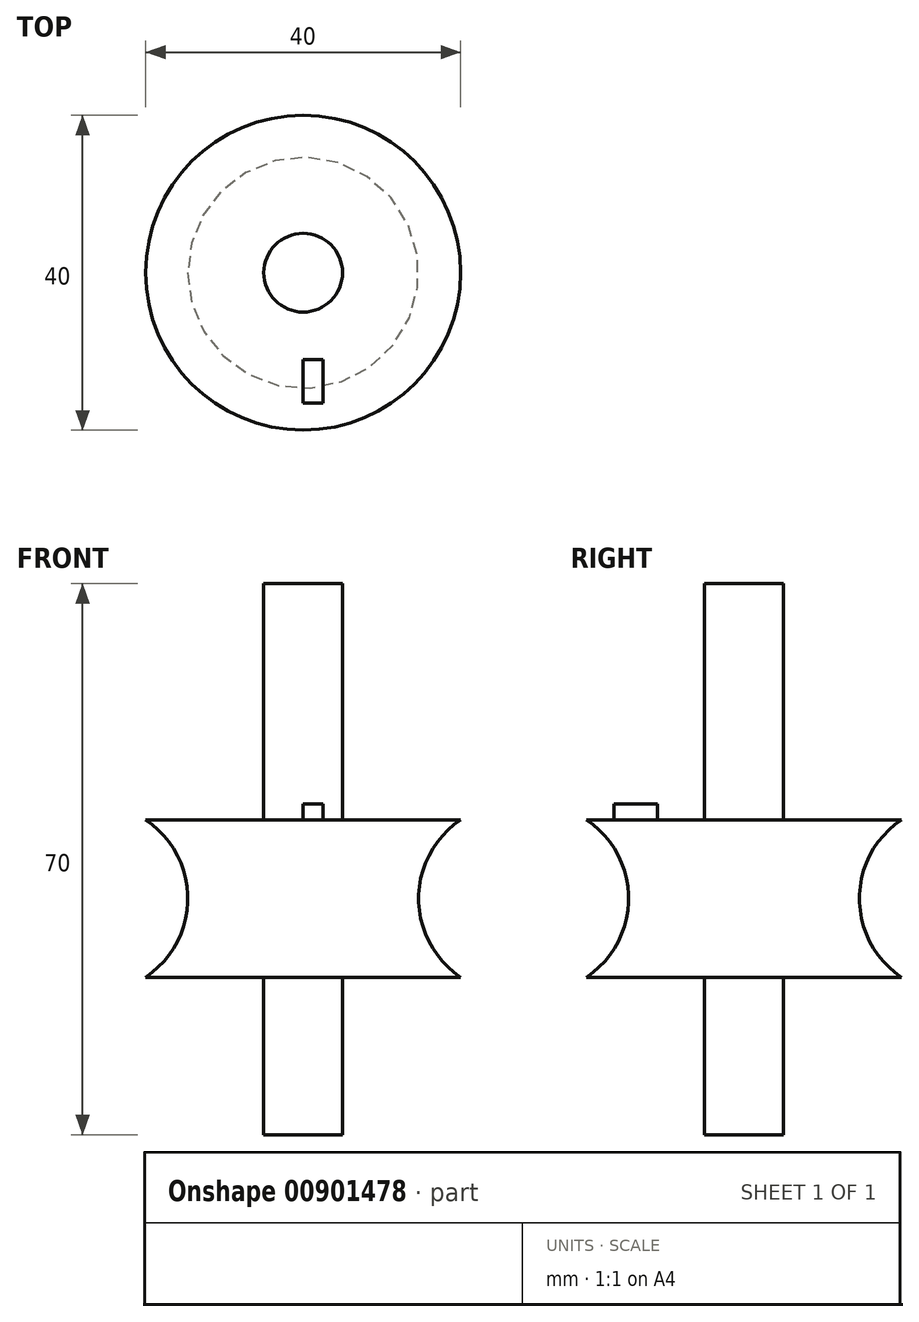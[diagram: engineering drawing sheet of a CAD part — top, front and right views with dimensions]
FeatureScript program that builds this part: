
annotation { "Feature Type Name" : "Feature", "Feature Type Description" : "" }
export const myFeature = defineFeature(function(context is Context, id is Id, definition is map)
    precondition{}
    {
        {
            var Q0;
            Q0=qCreatedBy(makeId("Front.planeOp"),FACE);
            var sketch = newSketch(context, id + "F0", { "sketchPlane" : qUnion([Q0])});
            skLineSegment(sketch, "E0", {"start": v(0, 0) * mm, "end": v(0, 70) * mm});
            skLineSegment(sketch, "E1", {"start": v(0, 70) * mm, "end": v(5, 70) * mm});
            skLineSegment(sketch, "E2", {"start": v(5, 70) * mm, "end": v(5, 40) * mm});
            skLineSegment(sketch, "E3", {"start": v(5, 40) * mm, "end": v(20, 40) * mm});
            skLineSegment(sketch, "E4", {"start": v(20, 40) * mm, "end": v(20, 20) * mm});
            skLineSegment(sketch, "E5", {"start": v(20, 20) * mm, "end": v(5, 20) * mm});
            skLineSegment(sketch, "E6", {"start": v(5, 20) * mm, "end": v(5, 0) * mm});
            skLineSegment(sketch, "E7", {"start": v(5, 0) * mm, "end": v(0, 0) * mm});
            skArc(sketch, "E8", {"start": v(20, 40) * mm, "mid": v(14.66, 30) * mm, "end": v(20, 20) * mm});
            skSolve(sketch);
        }
        {
            var Q0;
            Q0=makeQuery(id+"F0.imprint","IMPRINT",FACE,{"disambiguationData":[TD([[makeQuery(id+"F0.imprint","IMPRINT",EDGE,{"derivedFrom":sQuery(id+"F0.wireOp",EDGE,"E0")}),-1.0]])]});
            var Q1;
            Q1=sQuery(id+"F0.wireOp",EDGE,"E0");
            revolve(context, id + "F1", {"surfaceOperationType" : NewSurfaceOperationType.NEW, "entities" : qUnion([Q0]), "axis" : qUnion([Q1]), "revolveType" : RevolveType.FULL});
        }
        {
            var Q0;
            Q0=makeQuery(id+"F1.opRevolve","SWEPT_FACE",FACE,{"disambiguationData":[OSD([sQuery(id+"F0.wireOp",EDGE,"E3")])]});
            var sketch = newSketch(context, id + "F2", { "sketchPlane" : qUnion([Q0])});
            skLineSegment(sketch, "E9.bottom", {"start": v(0, -11) * mm, "end": v(2.5, -11) * mm});
            skLineSegment(sketch, "E9.top", {"start": v(0, -16.54) * mm, "end": v(2.5, -16.54) * mm});
            skLineSegment(sketch, "E9.left", {"start": v(0, -11) * mm, "end": v(0, -16.54) * mm});
            skLineSegment(sketch, "E9.right", {"start": v(2.5, -11) * mm, "end": v(2.5, -16.54) * mm});
            skSolve(sketch);
        }
        {
            var Q0;
            Q0 = qSketchRegion(id + "F2", true);
            extrude(context, id + "F3", {"entities" : qUnion([Q0]), "operationType" : NewBodyOperationType.ADD, "depth" : 2 * mm, "offsetDistance" : 25 * mm});
        }
    });
